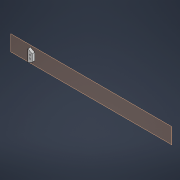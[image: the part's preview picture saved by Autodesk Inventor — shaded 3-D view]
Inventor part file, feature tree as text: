
AUTODESK INVENTOR PART (.ipt)
format: ipt  version: 2022 (Build 260153000, 153)  size: 123,904 bytes
history: native  units: in
note: dims shown in document units (in); Inventor stores cm internally (conversion verified against a paired STEP export)
features: other x5, reference x3, extrude x2, plane x1, sketch x1
ambient origin geometry x8: Origin, YZ Plane, XZ Plane, XY Plane, X Axis, Y Axis, Z Axis, Center Point
bodies: Solid1 (feature_tree)
feature tree (12):
  plane  "Work Plane1"
  sketch  "Sketch1"  dims[d0=0.1181in d1=0.1181in d2=0.374in d3=0.1063in d4=0.1063in d5=0.5in d6=0.315in d7=0.0in d8=0.315in d9=0.2362in d10=0.0in d11=0.0in]
  extrude  "Extrusion1"  Depth=0.1181in
  extrude  "Extrusion2"  Depth=0.2362in
  reference  "Reference1"
  reference  "Reference2"
  reference  "Reference3"
  other  "<userpath>\Documents\Bibble0\Bibble0.iam"
  other  "Bibble0.iam"
  other  "X Axis Cross:1"
  other  "MGN-12H:5"
  other  "Rail 400mm:1"
